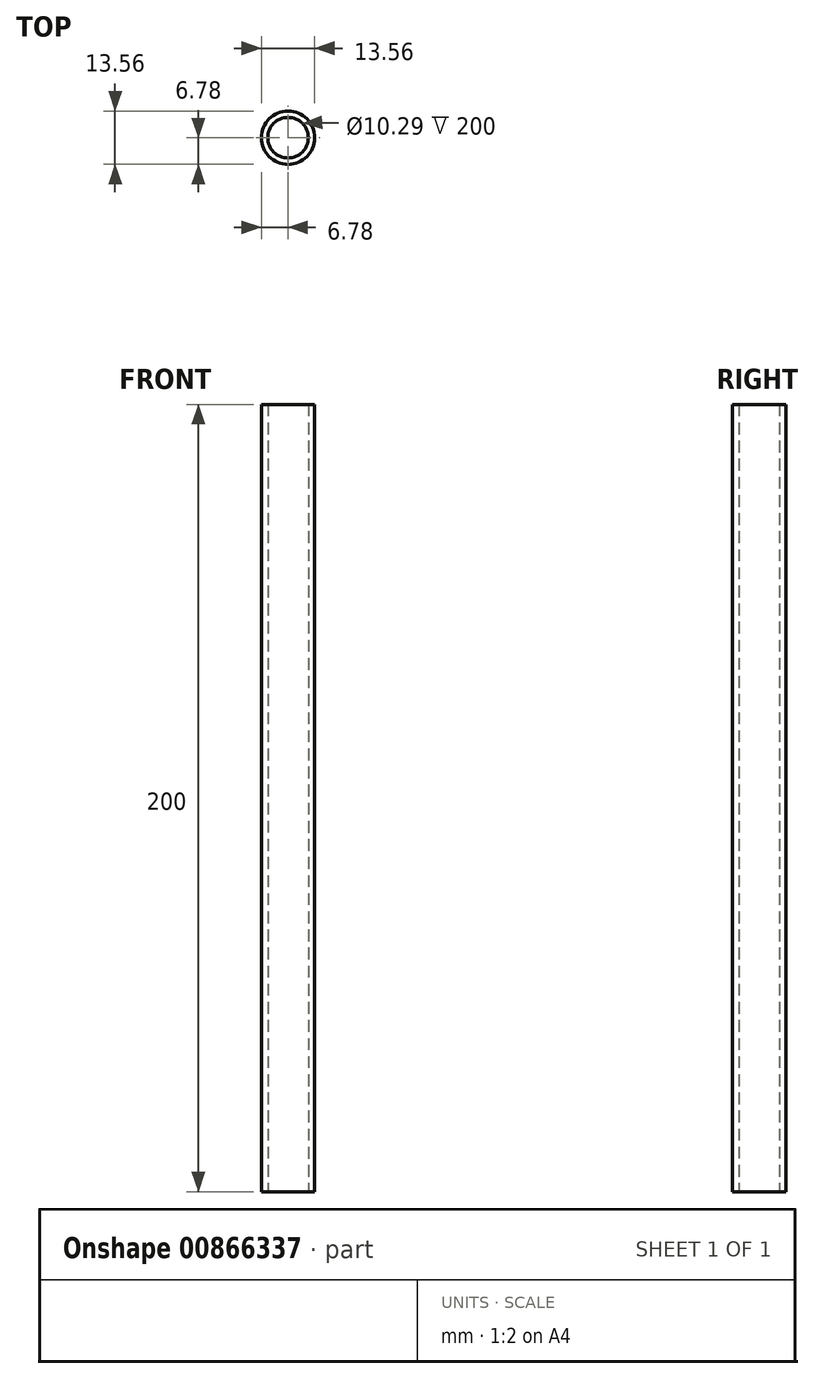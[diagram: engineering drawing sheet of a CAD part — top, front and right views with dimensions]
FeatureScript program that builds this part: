
annotation { "Feature Type Name" : "Feature", "Feature Type Description" : "" }
export const myFeature = defineFeature(function(context is Context, id is Id, definition is map)
    precondition{}
    {
        {
            var Q0;
            Q0=qCreatedBy(makeId("Top.planeOp"),FACE);
            var sketch = newSketch(context, id + "F0", { "sketchPlane" : qUnion([Q0])});
            skCircle(sketch, "E0", {"center": v(0, 0) * mm, "radius": 6.78 * mm});
            skCircle(sketch, "E1", {"center": v(0, 0) * mm, "radius": 5.15 * mm});
            skSolve(sketch);
        }
        {
            var Q0;
            Q0=makeQuery(id+"F0.imprint","IMPRINT",FACE,{"disambiguationData":[TD([[makeQuery(id+"F0.imprint","IMPRINT",EDGE,{"derivedFrom":sQuery(id+"F0.wireOp",EDGE,"E0")}),1.0]])]});
            extrude(context, id + "F1", {"entities" : qUnion([Q0]), "depth" : 200 * mm, "offsetDistance" : 25 * mm});
        }
    });
